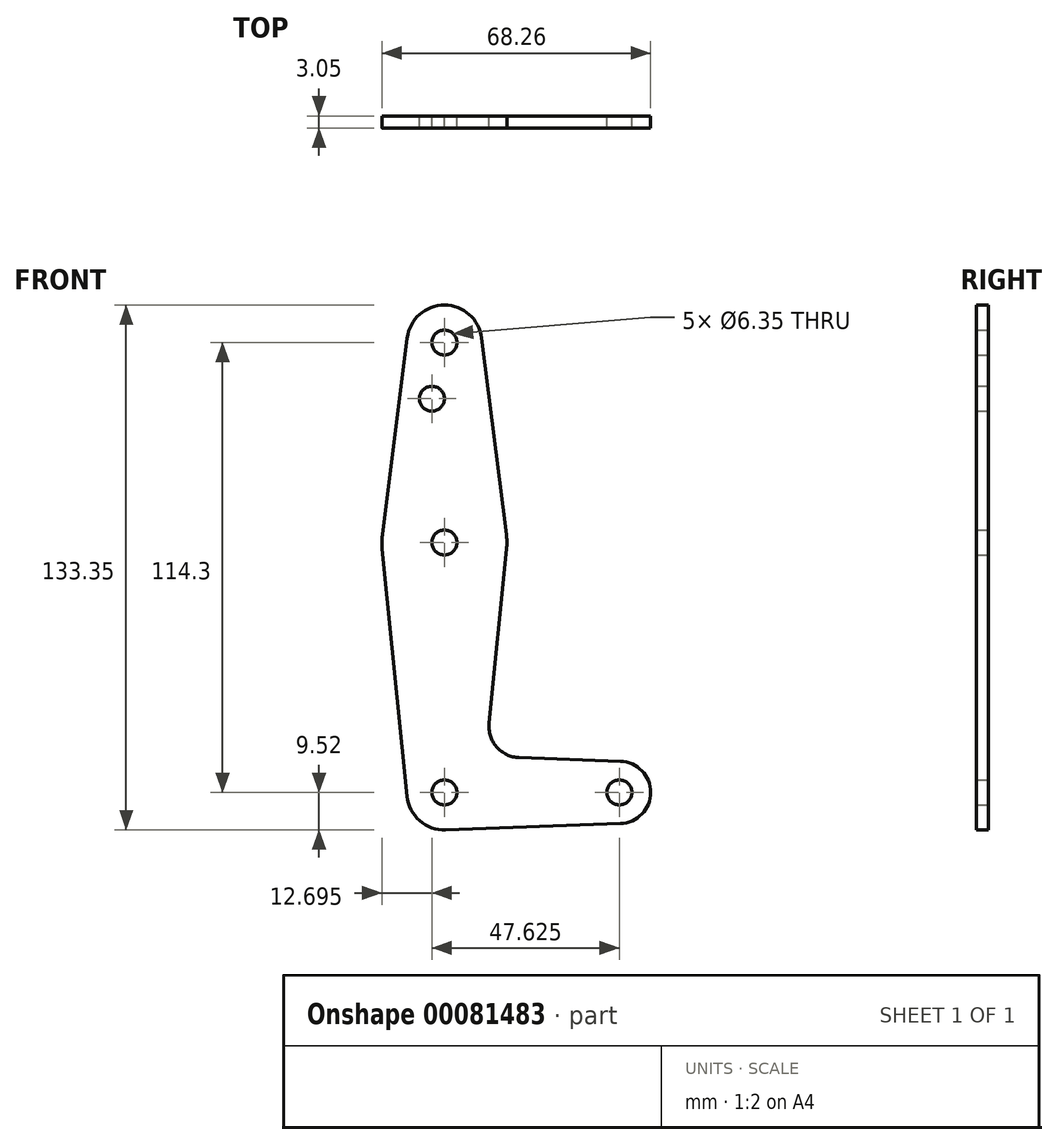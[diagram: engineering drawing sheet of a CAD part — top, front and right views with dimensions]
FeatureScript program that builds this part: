
annotation { "Feature Type Name" : "Feature", "Feature Type Description" : "" }
export const myFeature = defineFeature(function(context is Context, id is Id, definition is map)
    precondition{}
    {
        {
            var Q0;
            Q0=qCreatedBy(makeId("Front.planeOp"),FACE);
            var sketch = newSketch(context, id + "F0", { "sketchPlane" : qUnion([Q0])});
            skLineSegment(sketch, "E0", {"start": v(0, 0) * mm, "end": v(44.45, 0) * mm, "construction": true});
            skLineSegment(sketch, "E1", {"start": v(0, 0) * mm, "end": v(0, 114.3) * mm, "construction": true});
            skCircle(sketch, "E2", {"center": v(0, 0) * mm, "radius": 9.53 * mm});
            skCircle(sketch, "E3", {"center": v(44.45, 0) * mm, "radius": 7.94 * mm});
            skCircle(sketch, "E4", {"center": v(0, 63.5) * mm, "radius": 15.88 * mm});
            skCircle(sketch, "E5", {"center": v(0, 114.3) * mm, "radius": 9.52 * mm});
            skLineSegment(sketch, "E6", {"start": v(-9.45, 115.5) * mm, "end": v(-15.75, 65.48) * mm});
            skLineSegment(sketch, "E7", {"start": v(-15.8, 61.91) * mm, "end": v(-9.48, -0.95) * mm});
            skLineSegment(sketch, "E8", {"start": v(9.45, 115.5) * mm, "end": v(15.75, 65.48) * mm});
            skLineSegment(sketch, "E9", {"start": v(15.8, 61.91) * mm, "end": v(11.34, 17.6) * mm});
            skLineSegment(sketch, "E10", {"start": v(0.34, -9.52) * mm, "end": v(44.73, -7.93) * mm});
            skLineSegment(sketch, "E11", {"start": v(18.97, 8.85) * mm, "end": v(44.73, 7.93) * mm});
            skArc(sketch, "E12.filletArc", {"start": v(11.34, 17.6) * mm, "mid": v(13.26, 11.57) * mm, "end": v(18.97, 8.85) * mm});
            skCircle(sketch, "E13", {"center": v(-3.18, 100.03) * mm, "radius": 3.18 * mm});
            skCircle(sketch, "E14", {"center": v(0, 114.3) * mm, "radius": 3.18 * mm});
            skCircle(sketch, "E15", {"center": v(0, 63.5) * mm, "radius": 3.18 * mm});
            skCircle(sketch, "E16", {"center": v(0, 0) * mm, "radius": 3.18 * mm});
            skCircle(sketch, "E17", {"center": v(44.45, 0) * mm, "radius": 3.18 * mm});
            skSolve(sketch);
        }
        {
            var Q0;
            {var subQ0=sQuery(id+"F0.wireOp",EDGE,"E7");Q0=makeQuery(id+"F0.imprint","IMPRINT",FACE,{"disambiguationData":[TD([[makeQuery(id+"F0.imprint","IMPRINT",EDGE,{"derivedFrom":subQ0}),1.0]])]});}
            var Q1;
            Q1=makeQuery(id+"F0.imprint","IMPRINT",FACE,{"disambiguationData":[TD([[makeQuery(id+"F0.imprint","IMPRINT",EDGE,{"derivedFrom":sQuery(id+"F0.wireOp",EDGE,"E15")}),-1.0]])]});
            var Q2;
            {var subQ1=sQuery(id+"F0.wireOp",EDGE,"E6");Q2=makeQuery(id+"F0.imprint","IMPRINT",FACE,{"disambiguationData":[TD([[makeQuery(id+"F0.imprint","IMPRINT",EDGE,{"derivedFrom":subQ1}),1.0]])]});}
            var Q3;
            Q3=makeQuery(id+"F0.imprint","IMPRINT",FACE,{"disambiguationData":[TD([[makeQuery(id+"F0.imprint","IMPRINT",EDGE,{"derivedFrom":sQuery(id+"F0.wireOp",EDGE,"E14")}),-1.0]])]});
            var Q4;
            Q4=makeQuery(id+"F0.imprint","IMPRINT",FACE,{"disambiguationData":[TD([[makeQuery(id+"F0.imprint","IMPRINT",EDGE,{"derivedFrom":sQuery(id+"F0.wireOp",EDGE,"E16")}),-1.0]])]});
            var Q5;
            Q5=makeQuery(id+"F0.imprint","IMPRINT",FACE,{"disambiguationData":[TD([[makeQuery(id+"F0.imprint","IMPRINT",EDGE,{"derivedFrom":sQuery(id+"F0.wireOp",EDGE,"E17")}),-1.0]])]});
            extrude(context, id + "F1", {"entities" : qUnion([Q0, Q1, Q2, Q3, Q4, Q5]), "depth" : 3.05 * mm});
        }
    });
